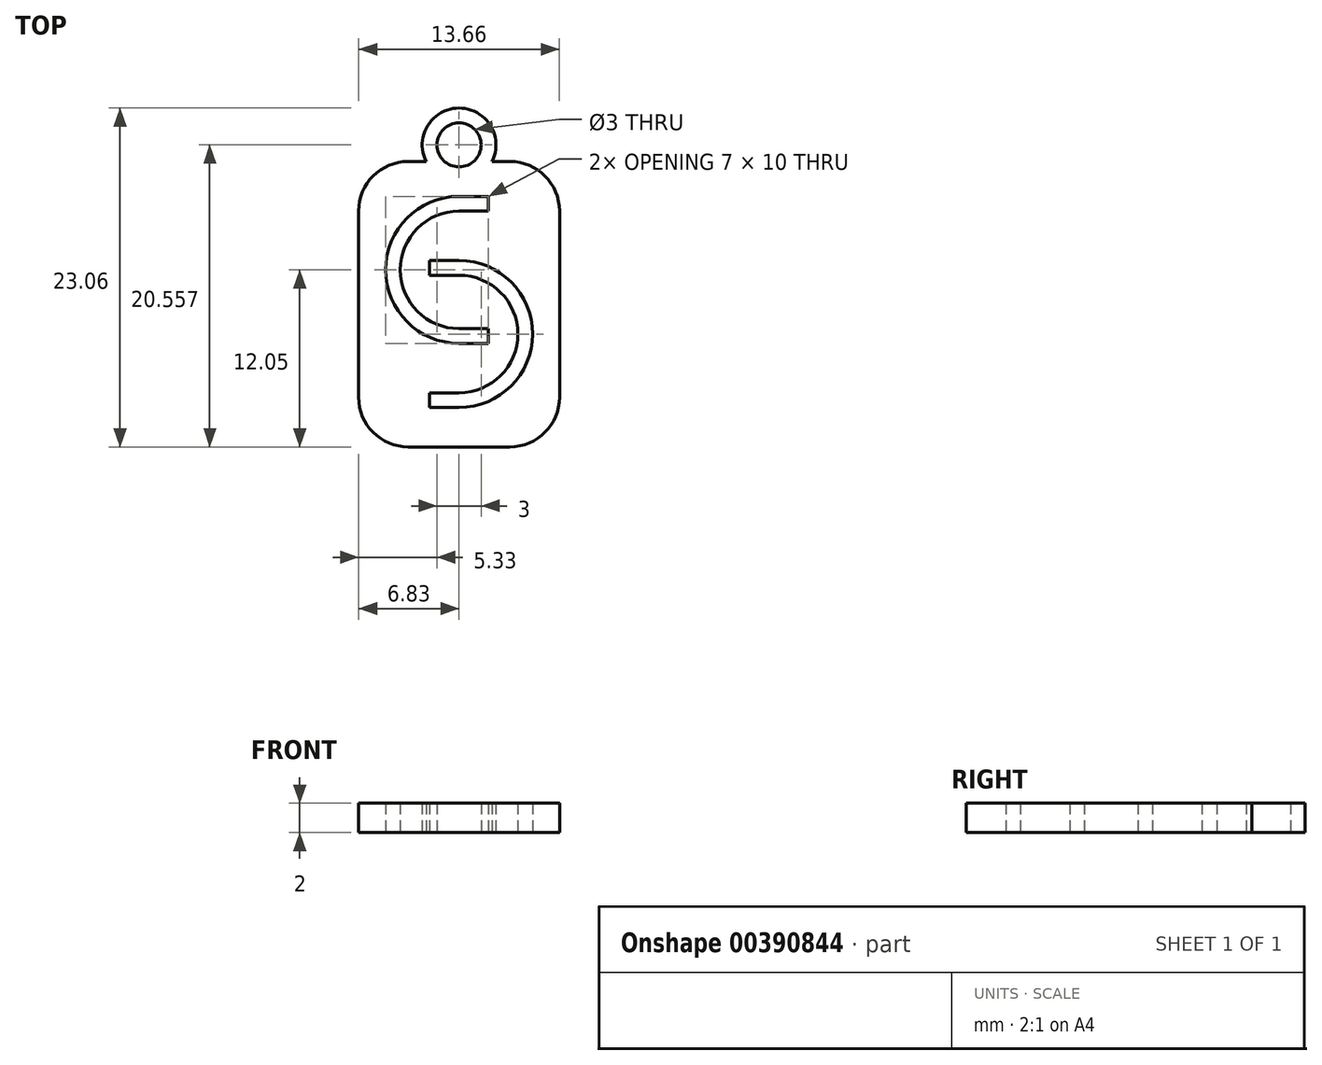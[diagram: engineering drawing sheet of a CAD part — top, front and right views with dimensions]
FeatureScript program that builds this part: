
annotation { "Feature Type Name" : "Feature", "Feature Type Description" : "" }
export const myFeature = defineFeature(function(context is Context, id is Id, definition is map)
    precondition{}
    {
        {
            var Q0;
            Q0=qCreatedBy(makeId("Top.planeOp"),FACE);
            var sketch = newSketch(context, id + "F0", { "sketchPlane" : qUnion([Q0])});
            skLineSegment(sketch, "E0", {"start": v(0, 51.88) * mm, "end": v(0, -69) * mm, "construction": true});
            skLineSegment(sketch, "E1", {"start": v(81.06, 0) * mm, "end": v(-86.12, 0) * mm, "construction": true});
            skArc(sketch, "E2", {"start": v(0, 12.79) * mm, "mid": v(-5, 7.79) * mm, "end": v(0, 2.79) * mm});
            skArc(sketch, "E3", {"start": v(0, 11.79) * mm, "mid": v(-4, 7.79) * mm, "end": v(0, 3.79) * mm});
            skArc(sketch, "E4", {"start": v(0, -1.57) * mm, "mid": v(5, 3.43) * mm, "end": v(0, 8.43) * mm});
            skArc(sketch, "E5.trimOffspring", {"start": v(0, -0.57) * mm, "mid": v(4, 3.43) * mm, "end": v(0, 7.43) * mm});
            skLineSegment(sketch, "E6", {"start": v(0, 11.79) * mm, "end": v(2, 11.79) * mm});
            skLineSegment(sketch, "E7", {"start": v(2, 11.79) * mm, "end": v(2, 12.79) * mm});
            skLineSegment(sketch, "E8", {"start": v(2, 12.79) * mm, "end": v(0, 12.79) * mm});
            skLineSegment(sketch, "E9", {"start": v(0, 3.79) * mm, "end": v(2, 3.79) * mm});
            skLineSegment(sketch, "E10", {"start": v(2, 3.79) * mm, "end": v(2, 2.79) * mm});
            skLineSegment(sketch, "E11", {"start": v(2, 2.79) * mm, "end": v(0, 2.79) * mm});
            skLineSegment(sketch, "E12", {"start": v(-2, 8.43) * mm, "end": v(0, 8.43) * mm});
            skLineSegment(sketch, "E13", {"start": v(-2, 8.43) * mm, "end": v(-2, 7.43) * mm});
            skLineSegment(sketch, "E14", {"start": v(0, 7.43) * mm, "end": v(-2, 7.43) * mm});
            skLineSegment(sketch, "E15", {"start": v(0, -0.57) * mm, "end": v(-2, -0.57) * mm});
            skLineSegment(sketch, "E16", {"start": v(-2, -0.57) * mm, "end": v(-2, -1.57) * mm});
            skLineSegment(sketch, "E17", {"start": v(0, -1.57) * mm, "end": v(-2, -1.57) * mm});
            skLineSegment(sketch, "E18.bottom", {"start": v(-6.83, -4.26) * mm, "end": v(6.83, -4.26) * mm});
            skLineSegment(sketch, "E18.top", {"start": v(-6.83, 15.17) * mm, "end": v(-2.24, 15.17) * mm});
            skLineSegment(sketch, "E18.left", {"start": v(-6.83, -4.26) * mm, "end": v(-6.83, 15.17) * mm});
            skLineSegment(sketch, "E18.right", {"start": v(6.83, -4.26) * mm, "end": v(6.83, 15.17) * mm});
            skPoint(sketch, "E18.middle", {"position": v(0, 5.45) * mm});
            skLineSegment(sketch, "E19.trimOffspring", {"start": v(2.24, 15.17) * mm, "end": v(6.83, 15.17) * mm});
            skArc(sketch, "E20", {"start": v(2.24, 15.17) * mm, "mid": v(0, 18.8) * mm, "end": v(-2.24, 15.17) * mm});
            skCircle(sketch, "E21", {"center": v(0, 16.3) * mm, "radius": 1.5 * mm});
            skSolve(sketch);
        }
        {
            var Q0;
            Q0=makeQuery(id+"F0.imprint","IMPRINT",FACE,{"disambiguationData":[TD([[makeQuery(id+"F0.imprint","IMPRINT",EDGE,{"derivedFrom":sQuery(id+"F0.wireOp",EDGE,"E2")}),-1.0]])]});
            extrude(context, id + "F1", {"entities" : qUnion([Q0]), "depth" : 2 * mm});
        }
        {
            var Q0;
            Q0=makeQuery(id+"F1.opExtrude","SWEPT_EDGE",EDGE,{"disambiguationData":[OSD([sQuery(id+"F0.wireOp",EDGE,"E18.bottom"),sQuery(id+"F0.wireOp",EDGE,"E18.right")])]});
            var Q1;
            Q1=makeQuery(id+"F1.opExtrude","SWEPT_EDGE",EDGE,{"disambiguationData":[OSD([sQuery(id+"F0.wireOp",EDGE,"E18.top"),sQuery(id+"F0.wireOp",EDGE,"E18.left")])]});
            var Q2;
            Q2=makeQuery(id+"F1.opExtrude","SWEPT_EDGE",EDGE,{"disambiguationData":[OSD([sQuery(id+"F0.wireOp",EDGE,"E18.right"),sQuery(id+"F0.wireOp",EDGE,"E19.trimOffspring")])]});
            var Q3;
            Q3=makeQuery(id+"F1.opExtrude","SWEPT_EDGE",EDGE,{"disambiguationData":[OSD([sQuery(id+"F0.wireOp",EDGE,"E18.top"),sQuery(id+"F0.wireOp",EDGE,"E18.left")])]});
            var Q4;
            Q4=makeQuery(id+"F1.opExtrude","SWEPT_EDGE",EDGE,{"disambiguationData":[OSD([sQuery(id+"F0.wireOp",EDGE,"E18.bottom"),sQuery(id+"F0.wireOp",EDGE,"E18.right")])]});
            var Q5;
            Q5=makeQuery(id+"F1.opExtrude","SWEPT_EDGE",EDGE,{"disambiguationData":[OSD([sQuery(id+"F0.wireOp",EDGE,"E18.bottom"),sQuery(id+"F0.wireOp",EDGE,"E18.left")])]});
            fillet(context, id + "F2", {"entities" : qUnion([Q0, Q1, Q2, Q3, Q4, Q5]), "radius" : 3.37 * mm, "tangentPropagation" : true, "allowEdgeOverflow" : false});
        }
    });
